# Revit family: Detail-Composite Floor Decking-Steel & Tube-ComFlor 60_Temp_432c5b64-7f42-40fb-bcd6-3aa84c70f018
name_source: partatom
category: Detail Items
revit_build: Autodesk Revit 2016 (Build: 20160314_0715(x64)
units: mm (PartAtom-declared; Revit-internal decimal feet)

## family parameters
OmniClass Number = 23.25.10.17.11.11
OmniClass Title = Permanent Steel Forms
Rotate with component = No
Shared = No

## types (1)
- 0.75 Gauge
    CBICode = 3151
    CBIDescription = Composite construction of in situ concrete and permanent formwork
    ComFlor Design Software = http://www.comflor.nz
    ComFlor Technical Resources = http://www.comflor.nz
    Description = ComFlor® 60 profiled steel decking system by Steel & Tube.
    Design Instruction = All the design information in this CAD file should be cross referenced with ComFlor® technical literature and ComFlor® design software. Please refer to the terms and conditions in the Licence Agreement of the ComFlor® design software.
    Design Standard = Design code provisions are to either BS5950 and/or approved Eurocodes.
    Manufacturer = Steel & Tube
    ManufacturerName = Steel & Tube
    ManufacturerURL = http://www.steelandtube.co.nz
    Material Standard = Steel & Tube’s ComFlor® range of products are manufactured from materials conforming to AS1397:2011
    Model = ComFlor® 60
    ModifiedIssue_ANZRS = 20160512 $
    SpecificationDescription = ComFlor composite floor system
    SpecificationReference = 3151C
    Trademark = ComFlor® is a registered trade mark used in Australia and New Zealand under licence from Tata Steel UK Limited.
    Type Comments = 600mm cover width. Minimum yield strength of G550
    URL = http://www.comflor.nz
    Uniclass2015Code = Ss_30_12_85_16
    Uniclass2015Title = Composite steel and concrete floor, roof or balcony deck systems
    Uniclass2015Version = 2015
    Unit Length = 300 mm
    Weight = 8.64 kg/m²

## geometry (parser evidence)
native form markers: Sweep x2
no freeform markers — native parametric forms only
